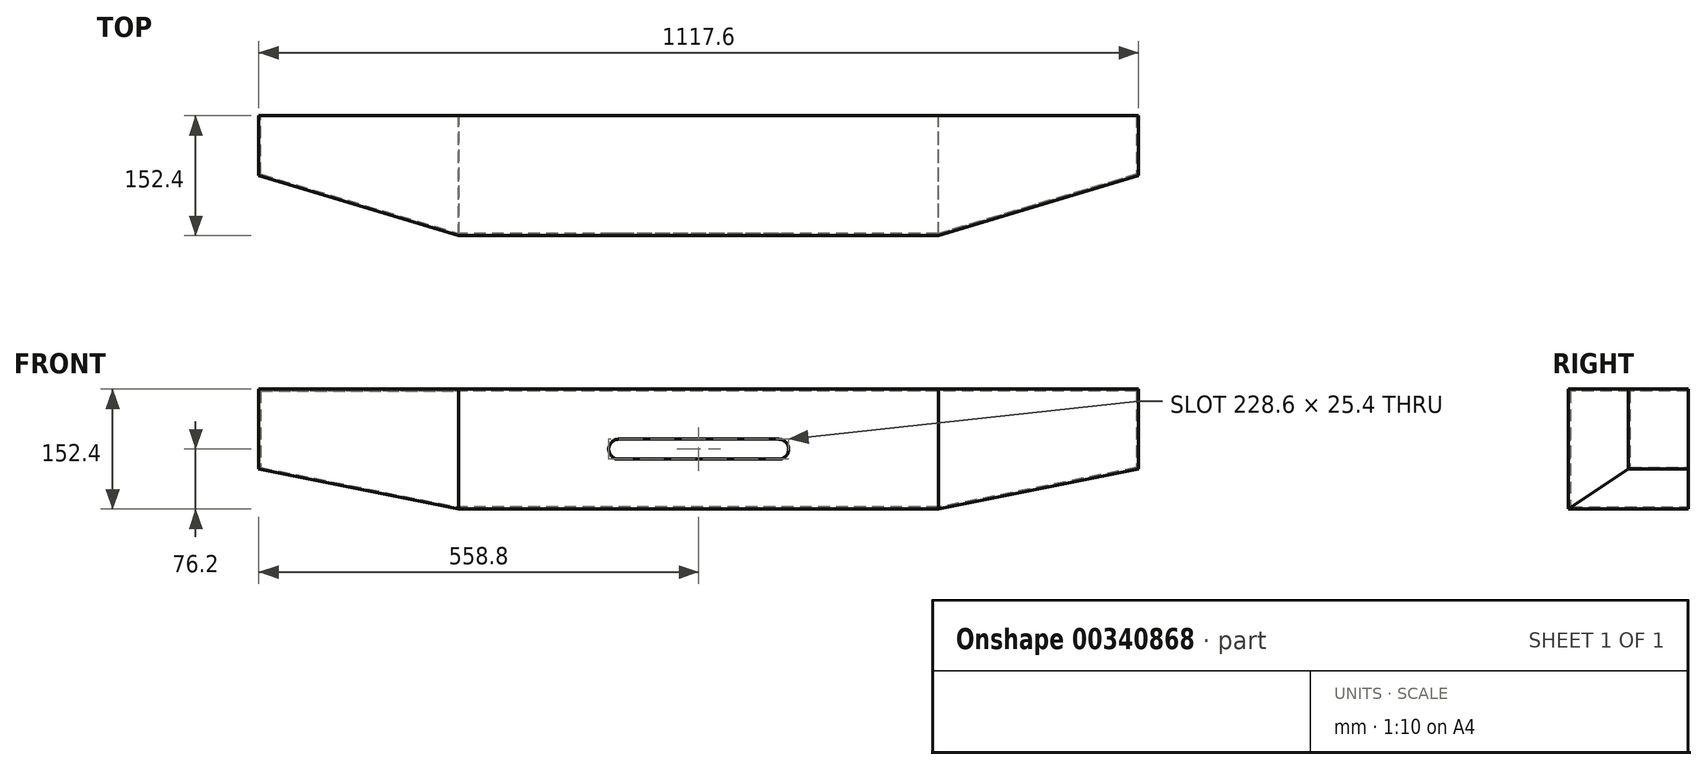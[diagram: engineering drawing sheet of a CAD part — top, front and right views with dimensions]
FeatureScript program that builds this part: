
annotation { "Feature Type Name" : "Feature", "Feature Type Description" : "" }
export const myFeature = defineFeature(function(context is Context, id is Id, definition is map)
    precondition{}
    {
        {
            var Q0;
            Q0=qCreatedBy(makeId("Top.planeOp"),FACE);
            var sketch = newSketch(context, id + "F0", { "sketchPlane" : qUnion([Q0])});
            skLineSegment(sketch, "E0.bottom", {"start": v(558.8, 76.2) * mm, "end": v(-558.8, 76.2) * mm});
            skLineSegment(sketch, "E0.top", {"start": v(304.8, -76.2) * mm, "end": v(-304.8, -76.2) * mm});
            skLineSegment(sketch, "E0.left", {"start": v(558.8, 76.2) * mm, "end": v(558.8, 0) * mm});
            skLineSegment(sketch, "E0.right", {"start": v(-558.8, 76.2) * mm, "end": v(-558.8, 0) * mm});
            skPoint(sketch, "E0.middle", {"position": v(0, 0) * mm});
            skLineSegment(sketch, "E1", {"start": v(-558.8, 0) * mm, "end": v(-304.8, -76.2) * mm});
            skLineSegment(sketch, "E2", {"start": v(558.8, 0) * mm, "end": v(304.8, -76.2) * mm});
            skPoint(sketch, "E3.orphan", {"position": v(-558.8, -76.2) * mm});
            skPoint(sketch, "E4.orphan", {"position": v(558.8, -76.2) * mm});
            skSolve(sketch);
        }
        {
            var Q0;
            Q0=qSketchRegion(id+"F0",true);
            extrude(context, id + "F1", {"entities" : qUnion([Q0]), "depth" : 152.4 * mm});
        }
        {
            var Q0;
            Q0=qCreatedBy(makeId("Front.planeOp"),FACE);
            cPlane(context, id + "F2", {"entities" : qUnion([Q0]), "cplaneType" : CPlaneType.OFFSET, "offset" : 76.2 * mm, "oppositeDirection" : true, "width" : 152.4 * mm, "height" : 152.4 * mm});
        }
        {
            var Q0;
            Q0=qCreatedBy(id+"F2.planeOp",FACE);
            var sketch = newSketch(context, id + "F3", { "sketchPlane" : qUnion([Q0])});
            skLineSegment(sketch, "E5", {"start": v(0, 0) * mm, "end": v(304.8, 0) * mm, "construction": true});
            skLineSegment(sketch, "E6", {"start": v(304.8, 0) * mm, "end": v(558.8, 0) * mm});
            skLineSegment(sketch, "E7", {"start": v(558.8, 0) * mm, "end": v(558.8, 50.8) * mm});
            skLineSegment(sketch, "E8", {"start": v(558.8, 50.8) * mm, "end": v(304.8, 0) * mm});
            skLineSegment(sketch, "E9", {"start": v(0, 0) * mm, "end": v(0, 160.49) * mm, "construction": true});
            skLineSegment(sketch, "E10", {"start": v(0, 0) * mm, "end": v(-304.8, 0) * mm, "construction": true});
            skLineSegment(sketch, "E11", {"start": v(-304.8, 0) * mm, "end": v(-558.8, 0) * mm});
            skLineSegment(sketch, "E12", {"start": v(-558.8, 0) * mm, "end": v(-558.8, 50.8) * mm});
            skLineSegment(sketch, "E13", {"start": v(-558.8, 50.8) * mm, "end": v(-304.8, 0) * mm});
            skSolve(sketch);
        }
        {
            var Q0;
            Q0=qSketchRegion(id+"F3",true);
            extrude(context, id + "F4", {"entities" : qUnion([Q0]), "operationType" : NewBodyOperationType.REMOVE, "depth" : 152.4 * mm});
        }
        {
            var Q0;
            Q0=makeQuery(id+"F1.opExtrude","SWEPT_FACE",FACE,{"disambiguationData":[OSD([sQuery(id+"F0.wireOp",EDGE,"E0.top")])]});
            var sketch = newSketch(context, id + "F5", { "sketchPlane" : qUnion([Q0])});
            skLineSegment(sketch, "E14.bottom", {"start": v(101.6, 88.9) * mm, "end": v(-101.6, 88.9) * mm});
            skLineSegment(sketch, "E14.top", {"start": v(101.6, 63.5) * mm, "end": v(-101.6, 63.5) * mm});
            skPoint(sketch, "E14.middle", {"position": v(0, 76.2) * mm});
            skPoint(sketch, "E14.middle.positionSnap0", {"position": v(304.8, 76.2) * mm});
            skPoint(sketch, "E14.centerSnap0", {"position": v(304.8, 76.2) * mm});
            skArc(sketch, "E15", {"start": v(101.6, 63.5) * mm, "mid": v(114.3, 76.2) * mm, "end": v(101.6, 88.9) * mm});
            skArc(sketch, "E16", {"start": v(-101.6, 88.9) * mm, "mid": v(-114.3, 76.2) * mm, "end": v(-101.6, 63.5) * mm});
            skSolve(sketch);
        }
        {
            var Q0;
            Q0=makeQuery(id+"F5.imprint","IMPRINT",FACE,{"disambiguationData":[TD([[makeQuery(id+"F5.imprint","IMPRINT",EDGE,{"derivedFrom":sQuery(id+"F5.wireOp",EDGE,"E14.bottom")}),1.0]])]});
            var Q1;
            Q1=sQuery(id+"F5.wireOp",EDGE,"E14.bottom");
            var Q2;
            Q2=sQuery(id+"F5.wireOp",EDGE,"E16");
            var Q3;
            Q3=sQuery(id+"F5.wireOp",EDGE,"E14.top");
            var Q4;
            Q4=sQuery(id+"F5.wireOp",EDGE,"E15");
            extrude(context, id + "F6", {"entities" : qUnion([Q0]), "operationType" : NewBodyOperationType.REMOVE, "surfaceEntities" : qUnion([Q1, Q2, Q3, Q4]), "endBound" : BoundingType.THROUGH_ALL, "oppositeDirection" : true, "depth" : 25.4 * mm});
        }
        {
            var Q0;
            Q0=makeQuery(id+"F1.opExtrude","SWEPT_FACE",FACE,{"disambiguationData":[OSD([sQuery(id+"F0.wireOp",EDGE,"E0.bottom")])]});
            shell(context, id + "F7", {"entities" : qUnion([Q0]), "thickness" : 2.54 * mm});
        }
        {
            var Q0;
            Q0=makeQuery(id+"F1.opExtrude","SWEPT_FACE",FACE,{"disambiguationData":[OSD([sQuery(id+"F0.wireOp",EDGE,"E0.bottom")])]});
            var Q1;
            Q1=makeQuery(id+"F7.opShell","OFFSET_FACE",FACE,{"disambiguationData":[OSD([sQuery(id+"F0.wireOp",EDGE,"E0.top")])]});
            extrude(context, id + "F8", {"entities" : qUnion([Q0]), "operationType" : NewBodyOperationType.REMOVE, "endBound" : BoundingType.UP_TO_SURFACE, "oppositeDirection" : true, "endBoundEntityFace" : qUnion([Q1]), "depth" : 149.22 * mm});
        }
    });
